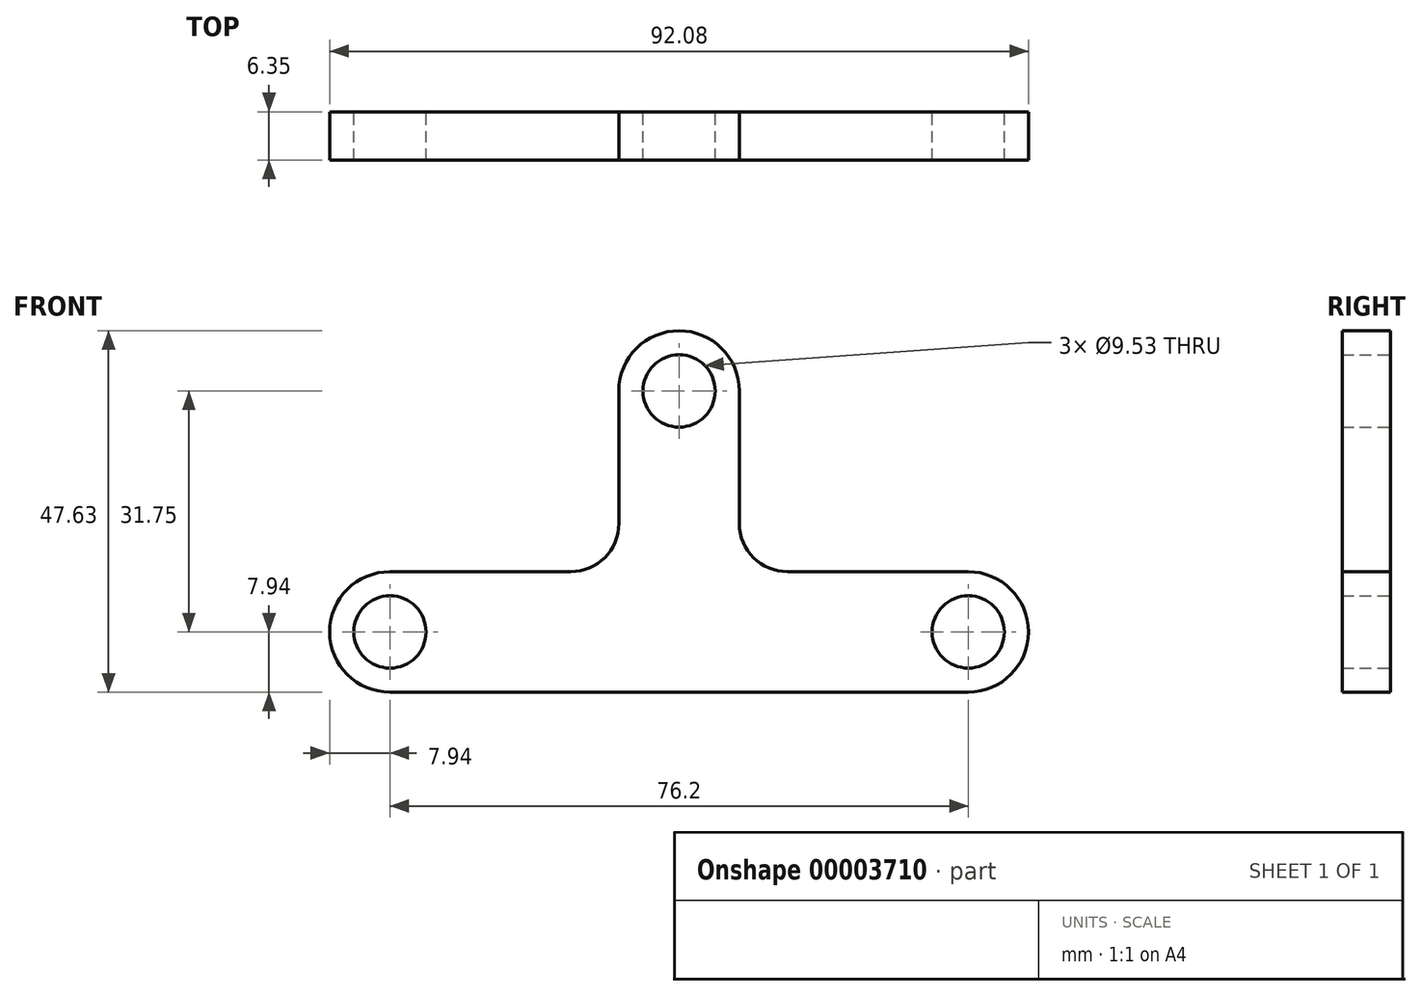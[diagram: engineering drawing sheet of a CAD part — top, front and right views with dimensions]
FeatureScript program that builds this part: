
annotation { "Feature Type Name" : "Feature", "Feature Type Description" : "" }
export const myFeature = defineFeature(function(context is Context, id is Id, definition is map)
    precondition{}
    {
        {
            var Q0;
            Q0=qCreatedBy(makeId("Front.planeOp"),FACE);
            var sketch = newSketch(context, id + "F0", { "sketchPlane" : qUnion([Q0])});
            skCircle(sketch, "E0", {"center": v(0, 0) * mm, "radius": 4.76 * mm});
            skCircle(sketch, "E1", {"center": v(38.1, 31.75) * mm, "radius": 4.76 * mm});
            skCircle(sketch, "E2", {"center": v(76.2, 0) * mm, "radius": 4.76 * mm});
            skArc(sketch, "E3", {"start": v(0, 7.94) * mm, "mid": v(-7.94, 0) * mm, "end": v(0, -7.94) * mm});
            skArc(sketch, "E4", {"start": v(76.2, -7.94) * mm, "mid": v(84.14, 0) * mm, "end": v(76.2, 7.94) * mm});
            skArc(sketch, "E5", {"start": v(46.04, 31.75) * mm, "mid": v(38.1, 39.69) * mm, "end": v(30.16, 31.75) * mm});
            skLineSegment(sketch, "E6", {"start": v(0, 7.94) * mm, "end": v(23.81, 7.94) * mm});
            skLineSegment(sketch, "E7", {"start": v(0, -7.94) * mm, "end": v(76.2, -7.94) * mm});
            skLineSegment(sketch, "E8", {"start": v(76.2, 7.94) * mm, "end": v(52.39, 7.94) * mm});
            skLineSegment(sketch, "E9", {"start": v(30.16, 31.75) * mm, "end": v(30.16, 14.29) * mm});
            skLineSegment(sketch, "E10", {"start": v(46.04, 31.75) * mm, "end": v(46.04, 14.29) * mm});
            skPoint(sketch, "E11.visualSharp", {"position": v(30.16, 7.94) * mm});
            skArc(sketch, "E11.filletArc", {"start": v(23.81, 7.94) * mm, "mid": v(28.3, 9.8) * mm, "end": v(30.16, 14.29) * mm});
            skPoint(sketch, "E12.visualSharp", {"position": v(46.04, 7.94) * mm});
            skArc(sketch, "E12.filletArc", {"start": v(46.04, 14.29) * mm, "mid": v(47.9, 9.8) * mm, "end": v(52.39, 7.94) * mm});
            skSolve(sketch);
        }
        {
            var Q0;
            Q0=qSketchRegion(id+"F0",true);
            extrude(context, id + "F1", {"entities" : qUnion([Q0]), "depth" : 6.35 * mm});
        }
    });
